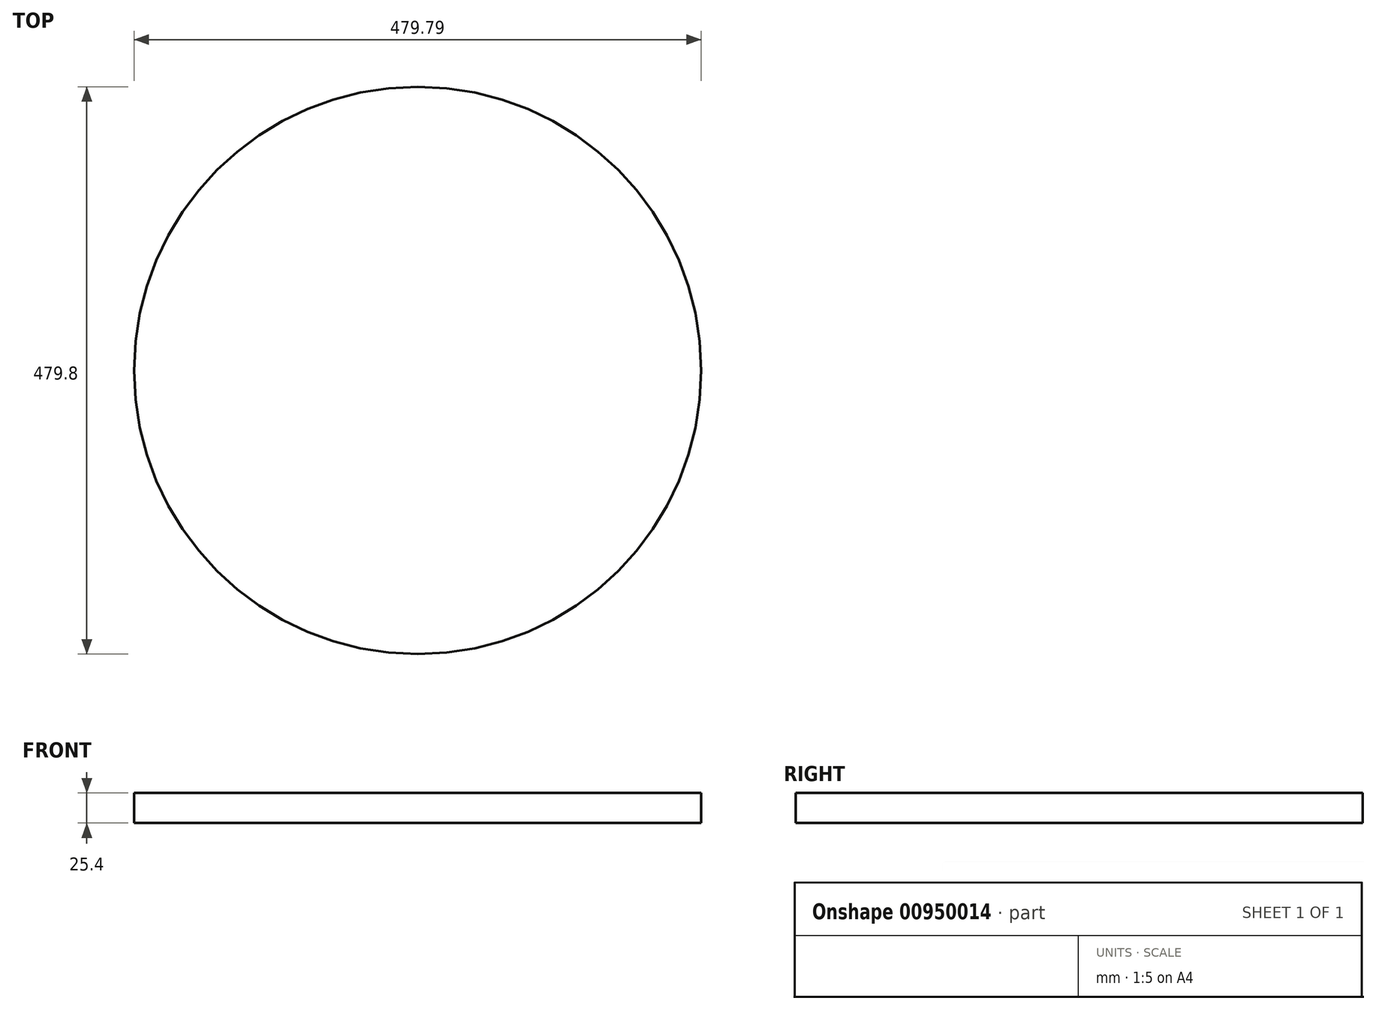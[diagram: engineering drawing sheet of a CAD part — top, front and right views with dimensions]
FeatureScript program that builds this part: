
annotation { "Feature Type Name" : "Feature", "Feature Type Description" : "" }
export const myFeature = defineFeature(function(context is Context, id is Id, definition is map)
    precondition{}
    {
        {
            var Q0;
            Q0=qCreatedBy(makeId("Top.planeOp"),FACE);
            var sketch = newSketch(context, id + "F0", { "sketchPlane" : qUnion([Q0])});
            skCircle(sketch, "E0", {"center": v(-148.34, 44.86) * mm, "radius": 239.9 * mm});
            skSolve(sketch);
        }
        {
            var Q0;
            Q0 = qSketchRegion(id + "F0", true);
            extrude(context, id + "F1", {"entities" : qUnion([Q0]), "depth" : 25.4 * mm, "offsetDistance" : 25.4 * mm});
        }
    });
